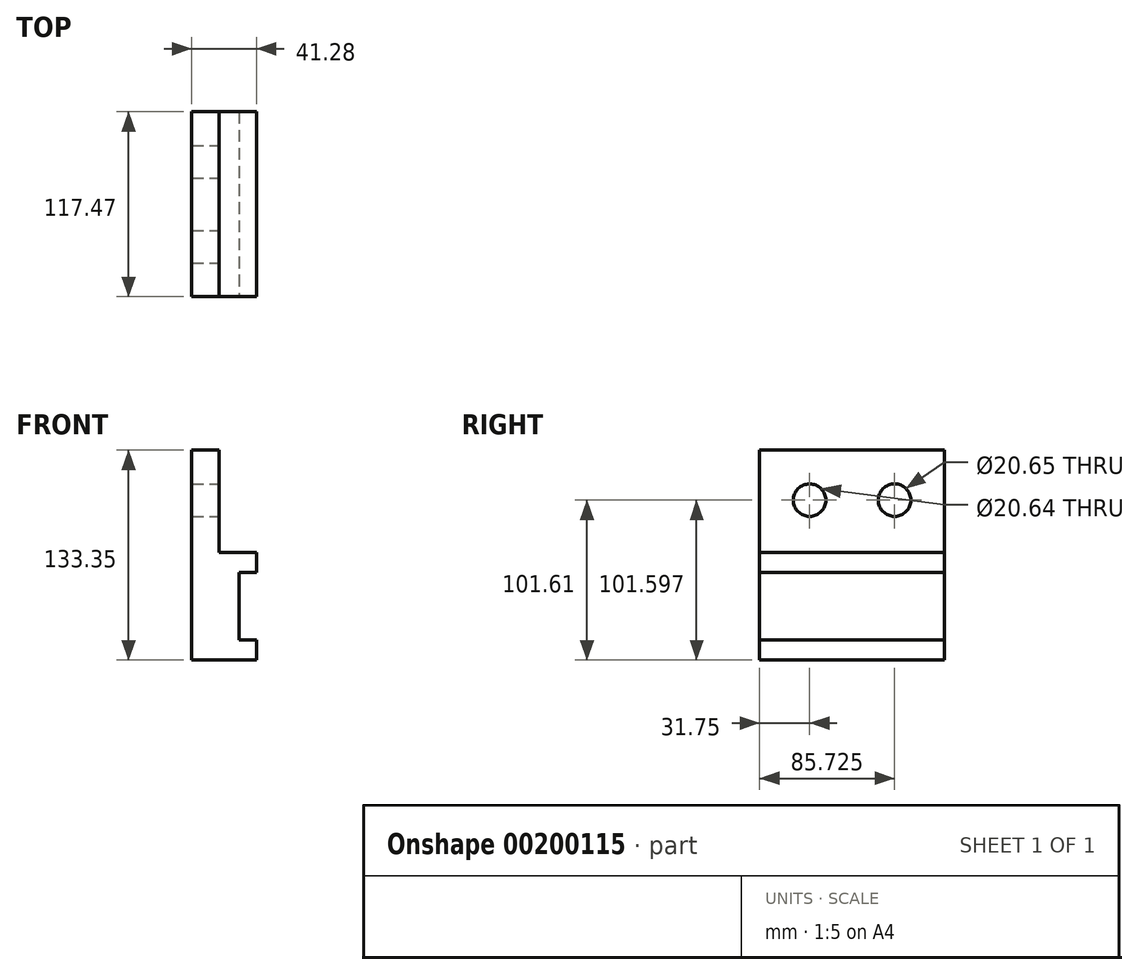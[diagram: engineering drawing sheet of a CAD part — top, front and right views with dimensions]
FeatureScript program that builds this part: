
annotation { "Feature Type Name" : "Feature", "Feature Type Description" : "" }
export const myFeature = defineFeature(function(context is Context, id is Id, definition is map)
    precondition{}
    {
        {
            var Q0;
            Q0=qCreatedBy(makeId("Front.planeOp"),FACE);
            var sketch = newSketch(context, id + "F0", { "sketchPlane" : qUnion([Q0])});
            skLineSegment(sketch, "E0.bottom", {"start": v(10.32, 48.78) * mm, "end": v(23.02, 48.78) * mm});
            skLineSegment(sketch, "E0.top", {"start": v(-7.14, -19.48) * mm, "end": v(23.02, -19.48) * mm});
            skLineSegment(sketch, "E0.left", {"start": v(-7.14, 48.78) * mm, "end": v(-7.14, -19.48) * mm});
            skLineSegment(sketch, "E0.right", {"start": v(23.02, 36.08) * mm, "end": v(23.02, -6.78) * mm});
            skLineSegment(sketch, "E1.bottom", {"start": v(23.02, -19.48) * mm, "end": v(34.14, -19.48) * mm});
            skLineSegment(sketch, "E1.top", {"start": v(23.02, -6.78) * mm, "end": v(34.14, -6.78) * mm});
            skLineSegment(sketch, "E1.right", {"start": v(34.14, -19.48) * mm, "end": v(34.14, -6.78) * mm});
            skLineSegment(sketch, "E2.bottom", {"start": v(23.02, 48.78) * mm, "end": v(34.14, 48.78) * mm});
            skLineSegment(sketch, "E2.top", {"start": v(23.02, 36.08) * mm, "end": v(34.14, 36.08) * mm});
            skLineSegment(sketch, "E2.right", {"start": v(34.14, 48.78) * mm, "end": v(34.14, 36.08) * mm});
            skLineSegment(sketch, "E3.top", {"start": v(-7.14, 113.87) * mm, "end": v(10.32, 113.87) * mm});
            skLineSegment(sketch, "E3.left", {"start": v(-7.14, 48.78) * mm, "end": v(-7.14, 113.87) * mm});
            skLineSegment(sketch, "E3.right", {"start": v(10.32, 48.78) * mm, "end": v(10.32, 113.87) * mm});
            skSolve(sketch);
        }
        {
            var Q0;
            Q0=makeQuery(id+"F0.imprint","IMPRINT",FACE,{"disambiguationData":[TD([[makeQuery(id+"F0.imprint","IMPRINT",EDGE,{"derivedFrom":sQuery(id+"F0.wireOp",EDGE,"E0.bottom")}),-1.0]])]});
            extrude(context, id + "F1", {"entities" : qUnion([Q0]), "oppositeDirection" : true, "depth" : 117.47 * mm});
        }
        {
            var Q0;
            Q0=makeQuery(id+"F1.opExtrude","SWEPT_FACE",FACE,{"disambiguationData":[OSD([sQuery(id+"F0.wireOp",EDGE,"E3.right")])]});
            var sketch = newSketch(context, id + "F2", { "sketchPlane" : qUnion([Q0])});
            skCircle(sketch, "E4", {"center": v(31.75, 82.12) * mm, "radius": 10.32 * mm});
            skCircle(sketch, "E5", {"center": v(85.72, 82.13) * mm, "radius": 10.33 * mm});
            skSolve(sketch);
        }
        {
            var Q0;
            Q0=makeQuery(id+"F2.imprint","IMPRINT",FACE,{"disambiguationData":[TD([[makeQuery(id+"F2.imprint","IMPRINT",EDGE,{"derivedFrom":sQuery(id+"F2.wireOp",EDGE,"E4")}),1.0]])]});
            var Q1;
            Q1=makeQuery(id+"F2.imprint","IMPRINT",FACE,{"disambiguationData":[TD([[makeQuery(id+"F2.imprint","IMPRINT",EDGE,{"derivedFrom":sQuery(id+"F2.wireOp",EDGE,"E5")}),1.0]])]});
            extrude(context, id + "F3", {"entities" : qUnion([Q0, Q1]), "operationType" : NewBodyOperationType.REMOVE, "oppositeDirection" : true, "depth" : 22.35 * mm});
        }
    });
